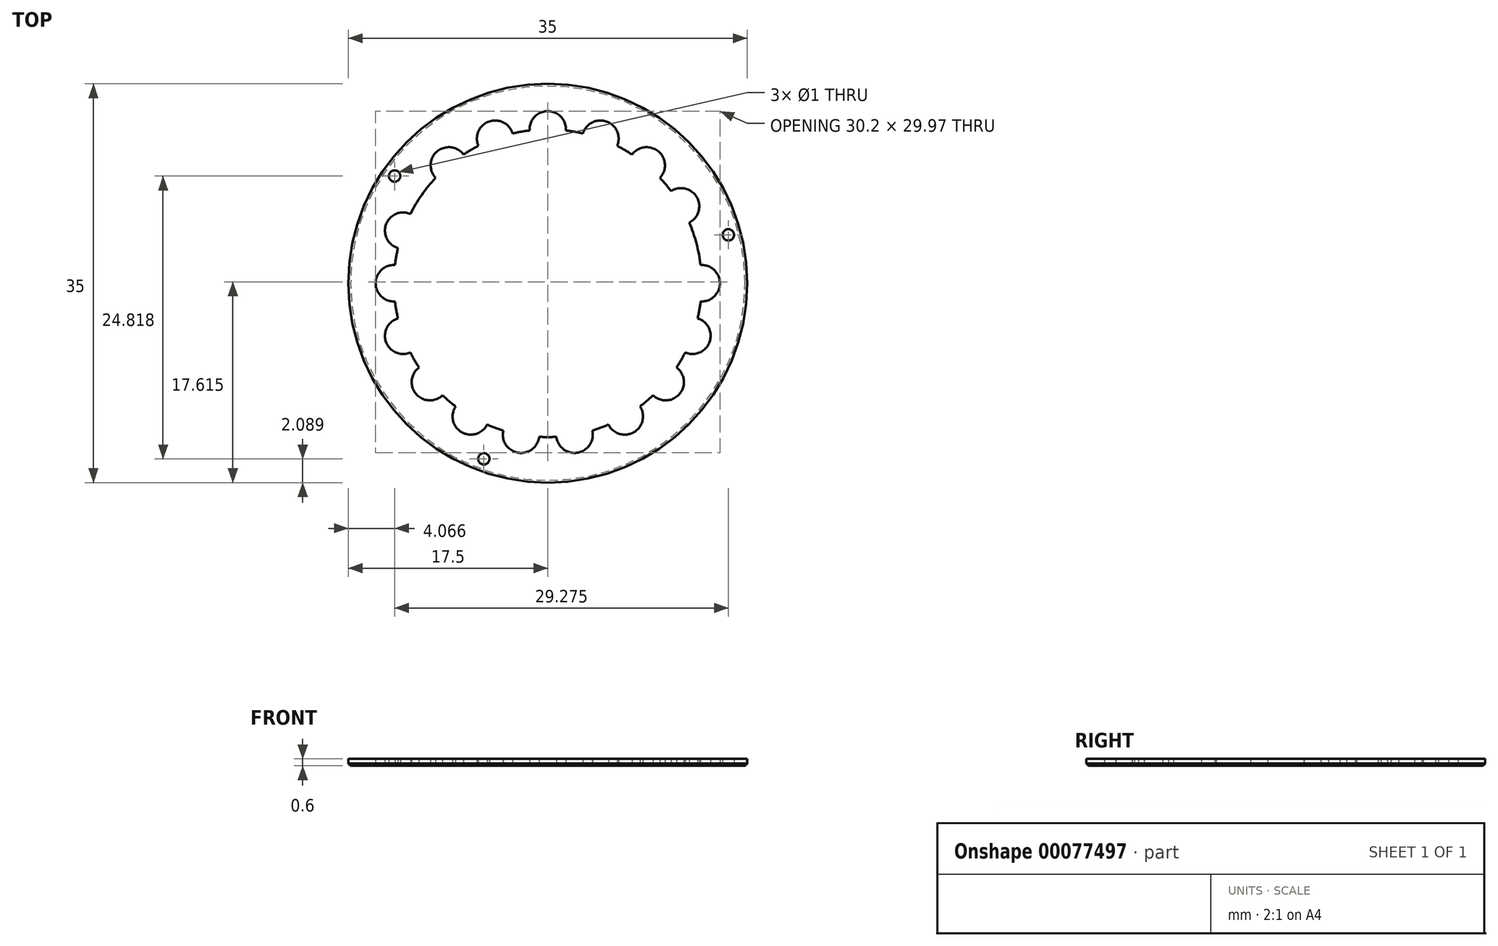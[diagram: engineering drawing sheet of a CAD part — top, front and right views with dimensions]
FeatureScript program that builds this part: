
annotation { "Feature Type Name" : "Feature", "Feature Type Description" : "" }
export const myFeature = defineFeature(function(context is Context, id is Id, definition is map)
    precondition{}
    {
        {
            var Q0;
            Q0=qCreatedBy(makeId("Top.planeOp"),FACE);
            var sketch = newSketch(context, id + "F0", { "sketchPlane" : qUnion([Q0])});
            skCircle(sketch, "E0", {"center": v(0, 0) * mm, "radius": 17.5 * mm});
            skCircle(sketch, "E1", {"center": v(0, 0) * mm, "radius": 13.5 * mm});
            skCircle(sketch, "E2", {"center": v(0, 0) * mm, "radius": 15.1 * mm, "construction": true});
            skCircle(sketch, "E3", {"center": v(13.5, 0) * mm, "radius": 1.6 * mm});
            skCircle(sketch, "E4.1.0", {"center": v(12.69, -4.62) * mm, "radius": 1.6 * mm});
            skCircle(sketch, "E4.2.0", {"center": v(10.34, -8.68) * mm, "radius": 1.6 * mm});
            skCircle(sketch, "E4.3.0", {"center": v(6.75, -11.7) * mm, "radius": 1.6 * mm});
            skCircle(sketch, "E4.4.0", {"center": v(2.34, -13.3) * mm, "radius": 1.6 * mm});
            skCircle(sketch, "E4.5.0", {"center": v(-2.34, -13.3) * mm, "radius": 1.6 * mm});
            skCircle(sketch, "E4.6.0", {"center": v(-6.75, -11.7) * mm, "radius": 1.6 * mm});
            skCircle(sketch, "E4.7.0", {"center": v(-10.34, -8.68) * mm, "radius": 1.6 * mm});
            skCircle(sketch, "E4.8.0", {"center": v(-12.69, -4.62) * mm, "radius": 1.6 * mm});
            skCircle(sketch, "E4.9.0", {"center": v(-13.5, 0) * mm, "radius": 1.6 * mm});
            skCircle(sketch, "E4.10.0", {"center": v(-12.69, 4.62) * mm, "radius": 1.6 * mm});
            skLineSegment(sketch, "E4.anchor1", {"start": v(0, 0) * mm, "end": v(13.5, 0) * mm, "construction": true});
            skLineSegment(sketch, "E4.anchor2", {"start": v(0, 0) * mm, "end": v(-12.69, 4.62) * mm, "construction": true});
            skCircle(sketch, "E5.1.0", {"center": v(-8.68, 10.34) * mm, "radius": 1.6 * mm});
            skLineSegment(sketch, "E5.anchor2", {"start": v(0, 0) * mm, "end": v(-8.68, 10.34) * mm, "construction": true});
            skCircle(sketch, "E6.1.0", {"center": v(-4.62, 12.69) * mm, "radius": 1.6 * mm});
            skCircle(sketch, "E6.2.0", {"center": v(0, 13.5) * mm, "radius": 1.6 * mm});
            skCircle(sketch, "E6.3.0", {"center": v(4.62, 12.69) * mm, "radius": 1.6 * mm});
            skCircle(sketch, "E6.4.0", {"center": v(8.68, 10.34) * mm, "radius": 1.6 * mm});
            skCircle(sketch, "E6.5.0", {"center": v(11.7, 6.75) * mm, "radius": 1.6 * mm});
            skLineSegment(sketch, "E6.anchor2", {"start": v(0, 0) * mm, "end": v(11.7, 6.75) * mm, "construction": true});
            skCircle(sketch, "E7", {"center": v(0, 0) * mm, "radius": 16.4 * mm, "construction": true});
            skLineSegment(sketch, "E8", {"start": v(0, 0) * mm, "end": v(15.84, 4.24) * mm, "construction": true});
            skCircle(sketch, "E9", {"center": v(15.84, 4.24) * mm, "radius": 0.5 * mm});
            skLineSegment(sketch, "E10", {"start": v(0, 0) * mm, "end": v(-5.6, -15.41) * mm, "construction": true});
            skLineSegment(sketch, "E11", {"start": v(0, 0) * mm, "end": v(-13.43, 9.4) * mm, "construction": true});
            skCircle(sketch, "E12", {"center": v(-13.43, 9.4) * mm, "radius": 0.5 * mm});
            skCircle(sketch, "E13", {"center": v(-5.6, -15.41) * mm, "radius": 0.5 * mm});
            skSolve(sketch);
        }
        {
            var Q0;
            Q0=makeQuery(id+"F0.imprint","IMPRINT",FACE,{"disambiguationData":[TD([[makeQuery(id+"F0.imprint","IMPRINT",EDGE,{"derivedFrom":sQuery(id+"F0.wireOp",EDGE,"E0")}),1.0]])]});
            extrude(context, id + "F1", {"entities" : qUnion([Q0]), "depth" : 0.6 * mm});
        }
        {
            var Q0;
            Q0=makeQuery(id+"F1.opExtrude","CAP_EDGE",EDGE,{"disambiguationData":[OSD([sQuery(id+"F0.wireOp",EDGE,"E0")])],"isStart":true});
            chamfer(context, id + "F2", {"entities" : qUnion([Q0]), "width" : 0.2 * mm, "tangentPropagation" : true});
        }
    });
